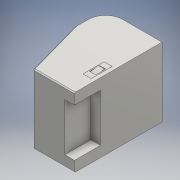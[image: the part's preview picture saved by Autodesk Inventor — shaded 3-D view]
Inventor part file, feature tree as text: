
AUTODESK INVENTOR PART (.ipt)
format: ipt  version: 2016 (Build 200138000, 138)  size: 254,464 bytes
history: native  units: mm
features: extrude x8, sketch x8, chamfer x2, fillet x1, projected_geometry x1
ambient origin geometry x8: Origin, YZ Plane, XZ Plane, XY Plane, X Axis, Y Axis, Z Axis, Center Point
bodies: Solid1 (feature_tree)
feature tree (20):
  extrude  "Extrusion1"  Depth=185.0mm
  extrude  "Extrusion2"  Depth=120.0mm
  extrude  "Extrusion3"  Depth=3.0mm
  extrude  "Extrusion4"  Depth=50.0mm
  chamfer  "Chamfer1"  Distance=3.0mm
  extrude  "Extrusion5"  Depth=3.0mm TaperAngle=0.0deg
  extrude  "Extrusion6"  Depth=10.0mm
  chamfer  "Chamfer2"  Distance=30.0mm
  extrude  "Extrusion7"  Depth=18.0mm
  fillet  "Fillet1"  Radius=4.0mm
  extrude  "Extrusion8"  Depth=4.0mm
  sketch  "Sketch1"  dims[d0=185.0mm d1=86.0mm]
  sketch  "Sketch2"  dims[d2=122.0mm d3=120.0mm]
  sketch  "Sketch3"  dims[d4=38.0mm d5=3.0mm]
  projected_geometry  "Projected Loop1"
  sketch  "Sketch4"  dims[d6=145.0mm d7=0.0mm d8=50.0mm]
  sketch  "Sketch5"  dims[d9=92.0mm]
  sketch  "Sketch6"  dims[d10=42.0mm]
  sketch  "Sketch7"  dims[d11=1.0mm d12=3.0mm d13=0.0mm]
  sketch  "Sketch9"  dims[d14=2.0mm d15=3.0mm d16=0.0mm d17=10.0mm d18=30.0mm d19=18.0mm d20=4.0mm d21=4.0mm d22=1.0mm d23=88.0mm d24=0.0mm d25=2.0mm d26=2.0mm d27=45.0deg d28=17.0mm d29=65.0mm d30=16.5mm d31=44.0mm d32=0.1mm d33=0.0mm d34=19.0mm d35=13.0mm d36=2.0mm d37=0.0mm d38=1.0mm d39=2.0mm d40=45.0deg d41=19.0mm d42=2.0mm d43=0.0mm d44=1.5mm d45=40.0mm d46=100.0mm d47=54.25mm d48=0.0mm]
